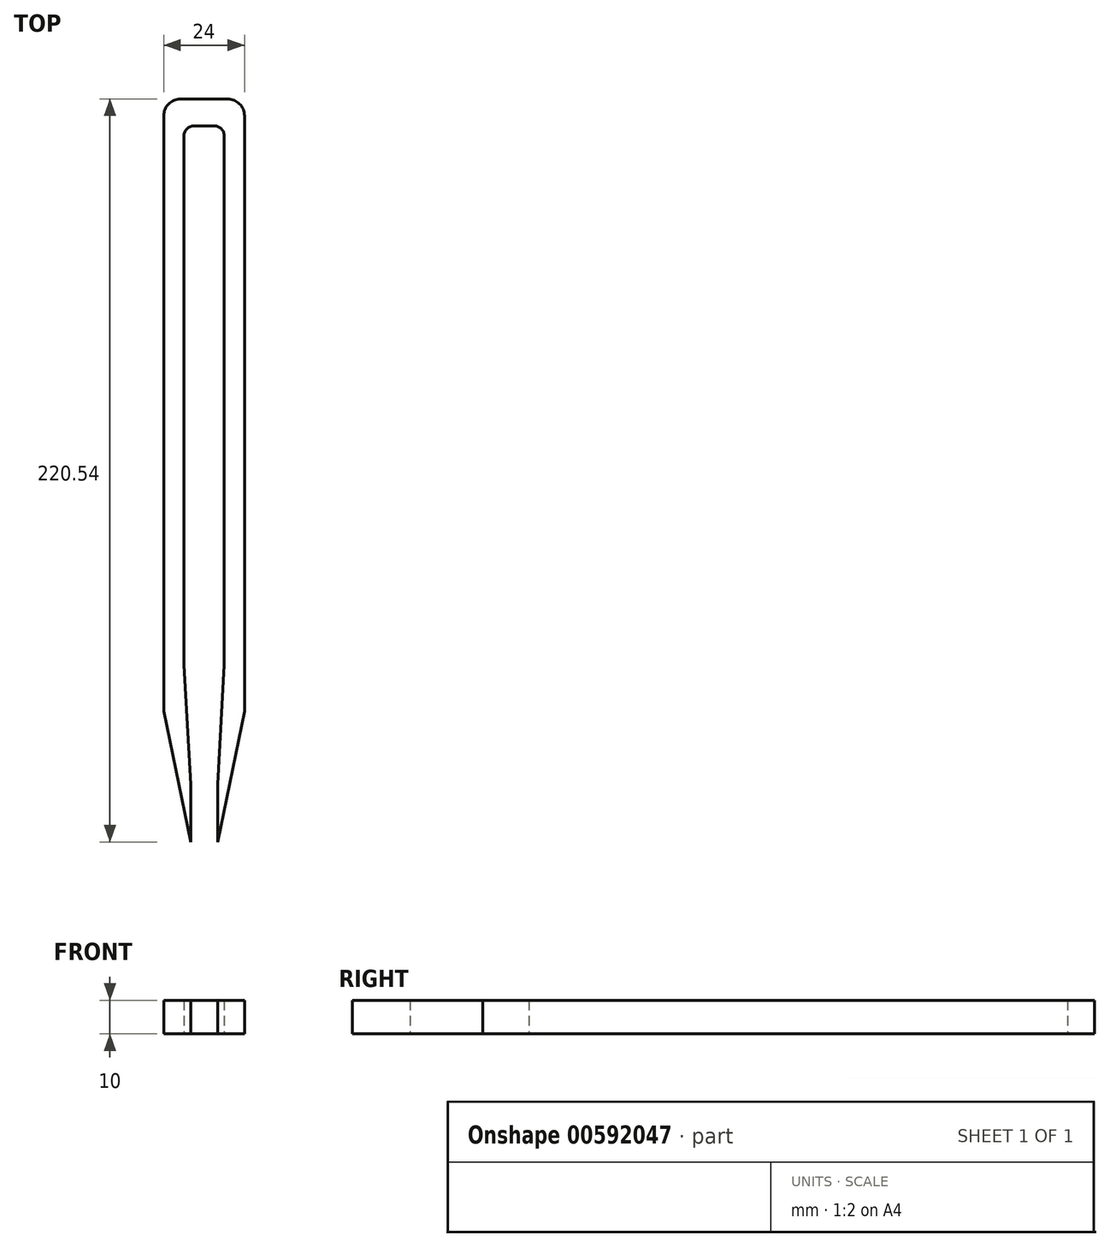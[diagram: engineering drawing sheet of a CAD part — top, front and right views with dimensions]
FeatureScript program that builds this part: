
annotation { "Feature Type Name" : "Feature", "Feature Type Description" : "" }
export const myFeature = defineFeature(function(context is Context, id is Id, definition is map)
    precondition{}
    {
        {
            var Q0;
            Q0=qCreatedBy(makeId("Top.planeOp"),FACE);
            var sketch = newSketch(context, id + "F0", { "sketchPlane" : qUnion([Q0])});
            skLineSegment(sketch, "E0", {"start": v(0, 105.43) * mm, "end": v(-6, 105.43) * mm});
            skLineSegment(sketch, "E1", {"start": v(-6, 105.43) * mm, "end": v(-6, -54.57) * mm});
            skLineSegment(sketch, "E2", {"start": v(-6, -54.57) * mm, "end": v(-4, -89.98) * mm});
            skLineSegment(sketch, "E3", {"start": v(-4, -89.98) * mm, "end": v(-4, -107.1) * mm});
            skLineSegment(sketch, "E4", {"start": v(-4, -107.1) * mm, "end": v(-12, -68.31) * mm});
            skLineSegment(sketch, "E5", {"start": v(-12, -68.31) * mm, "end": v(-12, 113.43) * mm});
            skLineSegment(sketch, "E6", {"start": v(-12, 113.43) * mm, "end": v(0, 113.43) * mm});
            skLineSegment(sketch, "E7.MirrorCS", {"start": v(12, 113.43) * mm, "end": v(0, 113.43) * mm});
            skLineSegment(sketch, "E8.MirrorCS", {"start": v(0, 105.43) * mm, "end": v(6, 105.43) * mm});
            skLineSegment(sketch, "E9.MirrorCS", {"start": v(6, 105.43) * mm, "end": v(6, -54.57) * mm});
            skLineSegment(sketch, "E10.MirrorCS", {"start": v(12, -68.31) * mm, "end": v(12, 113.43) * mm});
            skLineSegment(sketch, "E11.MirrorCS", {"start": v(6, -54.57) * mm, "end": v(4, -89.98) * mm});
            skLineSegment(sketch, "E12.MirrorCS", {"start": v(4, -89.98) * mm, "end": v(4, -107.1) * mm});
            skLineSegment(sketch, "E13.MirrorCS", {"start": v(4, -107.1) * mm, "end": v(12, -68.31) * mm});
            skSolve(sketch);
        }
        {
            var Q0;
            Q0=makeQuery(id+"F0.imprint","IMPRINT",FACE,{"disambiguationData":[TD([[makeQuery(id+"F0.imprint","IMPRINT",EDGE,{"derivedFrom":sQuery(id+"F0.wireOp",EDGE,"E0")}),-1.0]])]});
            extrude(context, id + "F1", {"entities" : qUnion([Q0]), "depth" : 10 * mm, "offsetDistance" : 25 * mm});
        }
        {
            var Q0;
            Q0=makeQuery(id+"F1.opExtrude","SWEPT_EDGE",EDGE,{"disambiguationData":[OSD([sQuery(id+"F0.wireOp",EDGE,"E8.MirrorCS"),sQuery(id+"F0.wireOp",EDGE,"E9.MirrorCS")])]});
            var Q1;
            Q1=makeQuery(id+"F1.opExtrude","SWEPT_EDGE",EDGE,{"disambiguationData":[OSD([sQuery(id+"F0.wireOp",EDGE,"E0"),sQuery(id+"F0.wireOp",EDGE,"E1")])]});
            fillet(context, id + "F2", {"entities" : qUnion([Q0, Q1]), "radius" : 3 * mm, "tangentPropagation" : true, "allowEdgeOverflow" : false});
        }
        {
            var Q0;
            Q0=makeQuery(id+"F1.opExtrude","SWEPT_EDGE",EDGE,{"disambiguationData":[OSD([sQuery(id+"F0.wireOp",EDGE,"E5"),sQuery(id+"F0.wireOp",EDGE,"E6")])]});
            var Q1;
            Q1=makeQuery(id+"F1.opExtrude","SWEPT_EDGE",EDGE,{"disambiguationData":[OSD([sQuery(id+"F0.wireOp",EDGE,"E7.MirrorCS"),sQuery(id+"F0.wireOp",EDGE,"E10.MirrorCS")])]});
            fillet(context, id + "F3", {"entities" : qUnion([Q0, Q1]), "radius" : 5 * mm, "tangentPropagation" : true, "allowEdgeOverflow" : false});
        }
    });
